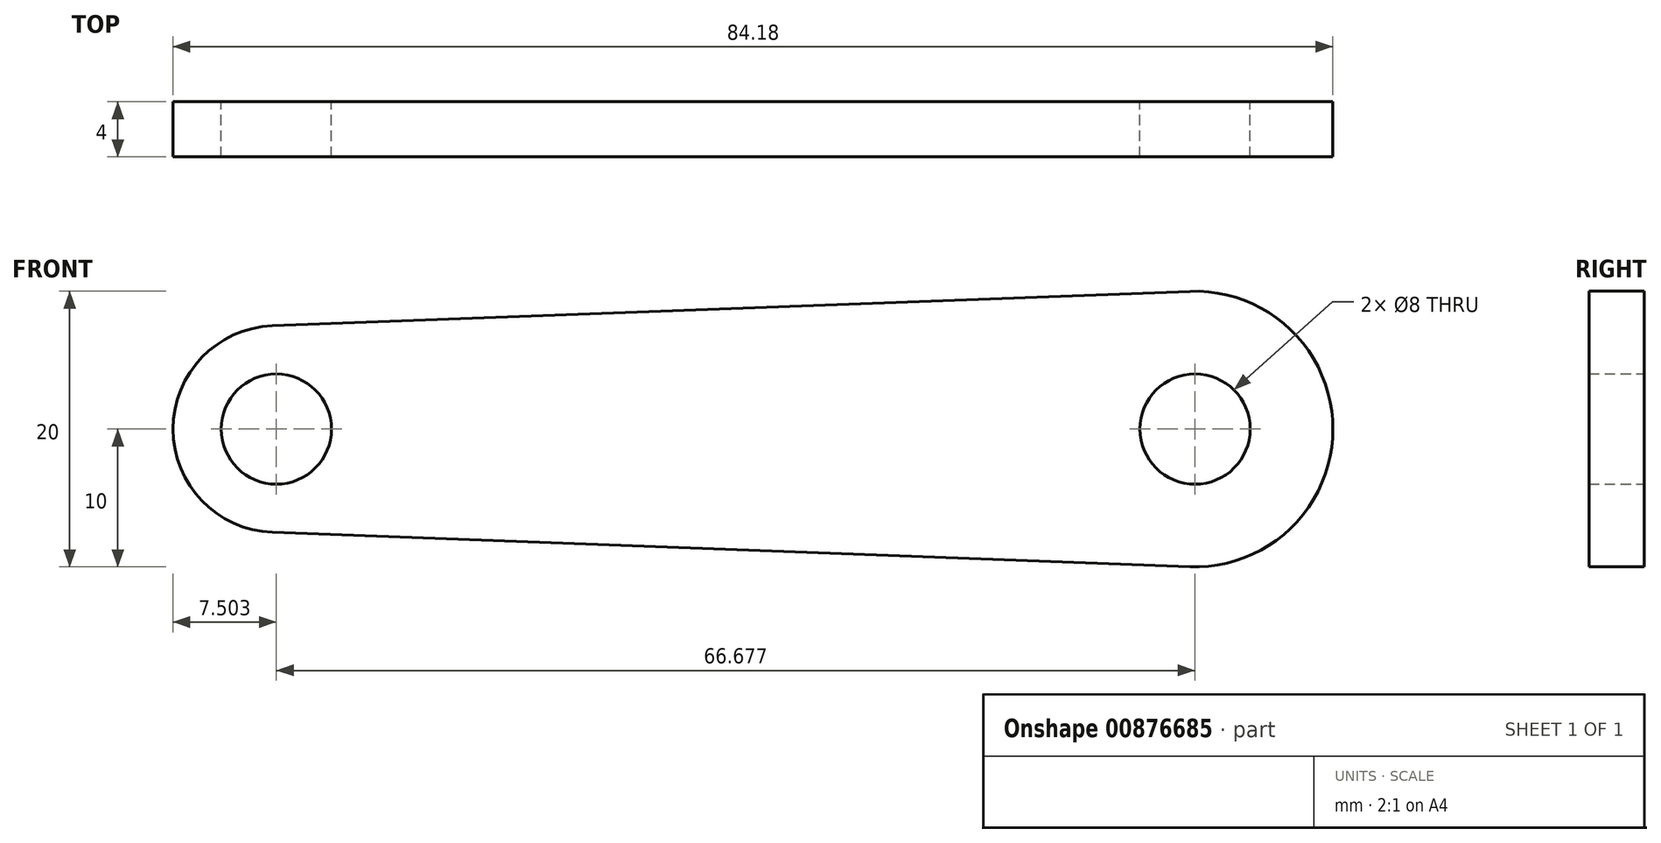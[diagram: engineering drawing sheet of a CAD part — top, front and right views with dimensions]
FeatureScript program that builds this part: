
annotation { "Feature Type Name" : "Feature", "Feature Type Description" : "" }
export const myFeature = defineFeature(function(context is Context, id is Id, definition is map)
    precondition{}
    {
        {
            var Q0;
            Q0=qCreatedBy(makeId("Front.planeOp"),FACE);
            var sketch = newSketch(context, id + "F0", { "sketchPlane" : qUnion([Q0])});
            skCircle(sketch, "E0", {"center": v(0, 0) * mm, "radius": 4 * mm});
            skCircle(sketch, "E1", {"center": v(-66.68, 0) * mm, "radius": 4 * mm});
            skArc(sketch, "E2", {"start": v(-0.37, -10) * mm, "mid": v(10, 0) * mm, "end": v(-0.37, 10) * mm});
            skArc(sketch, "E3", {"start": v(-66.96, 7.5) * mm, "mid": v(-74.18, 0) * mm, "end": v(-66.96, -7.5) * mm});
            skLineSegment(sketch, "E4", {"start": v(-66.96, 7.5) * mm, "end": v(-0.37, 10) * mm});
            skLineSegment(sketch, "E5", {"start": v(-66.96, -7.5) * mm, "end": v(-0.37, -10) * mm});
            skSolve(sketch);
        }
        {
            var Q0;
            Q0=makeQuery(id+"F0.imprint","IMPRINT",FACE,{"disambiguationData":[TD([[makeQuery(id+"F0.imprint","IMPRINT",EDGE,{"derivedFrom":sQuery(id+"F0.wireOp",EDGE,"E0")}),-1.0]])]});
            extrude(context, id + "F1", {"entities" : qUnion([Q0]), "depth" : 4 * mm, "offsetDistance" : 25 * mm});
        }
    });
